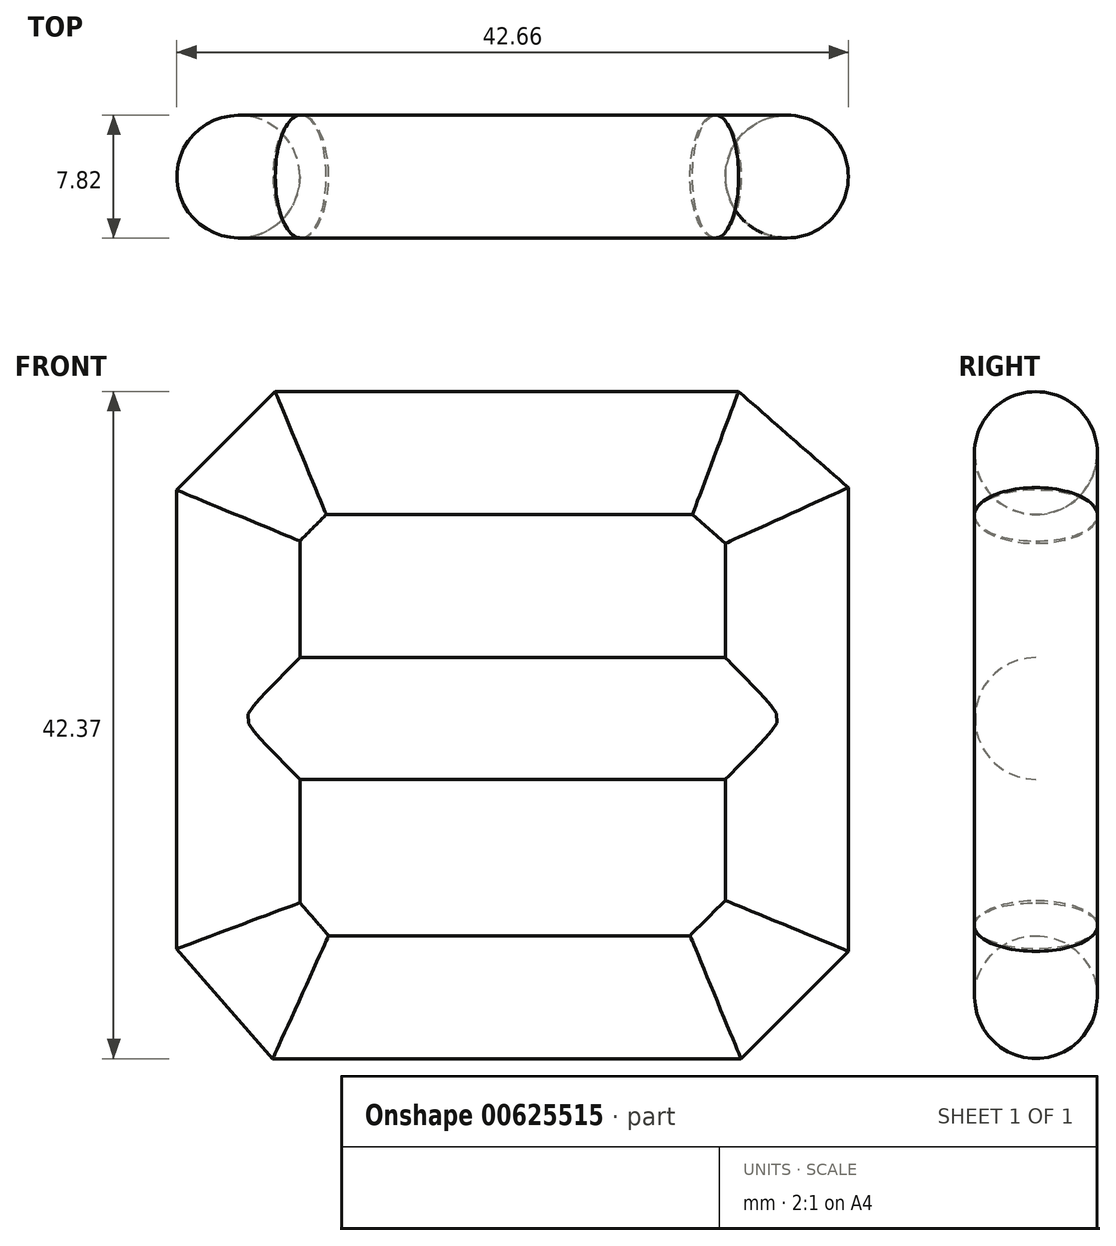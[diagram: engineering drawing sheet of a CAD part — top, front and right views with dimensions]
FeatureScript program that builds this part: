
annotation { "Feature Type Name" : "Feature", "Feature Type Description" : "" }
export const myFeature = defineFeature(function(context is Context, id is Id, definition is map)
    precondition{}
    {
        {
            var Q0;
            Q0=qCreatedBy(makeId("Top.planeOp"),FACE);
            var sketch = newSketch(context, id + "F0", { "sketchPlane" : qUnion([Q0])});
            skCircle(sketch, "E0", {"center": v(0, 0) * mm, "radius": 3.9 * mm});
            skSolve(sketch);
        }
        {
            var Q0;
            Q0=qCreatedBy(makeId("Front.planeOp"),FACE);
            var sketch = newSketch(context, id + "F1", { "sketchPlane" : qUnion([Q0])});
            skLineSegment(sketch, "E1", {"start": v(0, 0) * mm, "end": v(0, -13.17) * mm});
            skLineSegment(sketch, "E2", {"start": v(0, -13.17) * mm, "end": v(3.97, -17.7) * mm});
            skLineSegment(sketch, "E3", {"start": v(3.97, -17.7) * mm, "end": v(30.31, -17.7) * mm});
            skLineSegment(sketch, "E4", {"start": v(30.31, -17.7) * mm, "end": v(34.84, -13.17) * mm});
            skLineSegment(sketch, "E5", {"start": v(34.84, -13.17) * mm, "end": v(34.84, 0) * mm});
            skLineSegment(sketch, "E6", {"start": v(34.84, 0) * mm, "end": v(34.84, 12.89) * mm});
            skLineSegment(sketch, "E7", {"start": v(34.84, 12.89) * mm, "end": v(30.31, 16.85) * mm});
            skLineSegment(sketch, "E8", {"start": v(30.31, 16.85) * mm, "end": v(3.97, 16.85) * mm});
            skLineSegment(sketch, "E9", {"start": v(3.97, 16.85) * mm, "end": v(0, 12.89) * mm});
            skLineSegment(sketch, "E10", {"start": v(0, 12.89) * mm, "end": v(0, 0) * mm});
            skLineSegment(sketch, "E11", {"start": v(34.84, 0) * mm, "end": v(0, 0) * mm});
            skLineSegment(sketch, "E12", {"start": v(11.33, 16.85) * mm, "end": v(11.33, -17.7) * mm});
            skLineSegment(sketch, "E13", {"start": v(11.33, -17.7) * mm, "end": v(23.51, -17.7) * mm});
            skLineSegment(sketch, "E14", {"start": v(23.51, -17.7) * mm, "end": v(23.51, 16.85) * mm});
            skSolve(sketch);
        }
        {
            var Q0;
            Q0=makeQuery(id+"F0.imprint","IMPRINT",FACE,{"disambiguationData":[TD([[makeQuery(id+"F0.imprint","IMPRINT",EDGE,{"derivedFrom":sQuery(id+"F0.wireOp",EDGE,"E0")}),1.0]])]});
            var Q1;
            Q1=sQuery(id+"F1.wireOp",EDGE,"E10");
            var Q2;
            Q2=sQuery(id+"F1.wireOp",EDGE,"E9");
            var Q3;
            Q3=sQuery(id+"F1.wireOp",EDGE,"E8");
            var Q4;
            Q4=sQuery(id+"F1.wireOp",EDGE,"E7");
            var Q5;
            Q5=sQuery(id+"F1.wireOp",EDGE,"E6");
            var Q6;
            Q6=sQuery(id+"F1.wireOp",EDGE,"E5");
            var Q7;
            Q7=sQuery(id+"F1.wireOp",EDGE,"E4");
            var Q8;
            Q8=sQuery(id+"F1.wireOp",EDGE,"E3");
            var Q9;
            Q9=sQuery(id+"F1.wireOp",EDGE,"E2");
            var Q10;
            Q10=sQuery(id+"F1.wireOp",EDGE,"E1");
            sweep(context, id + "F2", {"profiles" : qUnion([Q0]), "path" : qUnion([Q1, Q2, Q3, Q4, Q5, Q6, Q7, Q8, Q9, Q10])});
        }
        {
            var Q0;
            Q0=qCreatedBy(makeId("Right.planeOp"),FACE);
            var sketch = newSketch(context, id + "F3", { "sketchPlane" : qUnion([Q0])});
            skCircle(sketch, "E15", {"center": v(0, 0) * mm, "radius": 3.87 * mm});
            skSolve(sketch);
        }
        {
            var Q0;
            Q0=qCreatedBy(makeId("Front.planeOp"),FACE);
            var sketch = newSketch(context, id + "F4", { "sketchPlane" : qUnion([Q0])});
            skLineSegment(sketch, "E16", {"start": v(0, 0) * mm, "end": v(35.13, 0) * mm});
            skSolve(sketch);
        }
        {
            var Q0;
            Q0 = qSketchRegion(id + "F3", true);
            var Q1;
            Q1=sQuery(id+"F4.wireOp",EDGE,"E16");
            sweep(context, id + "F5", {"operationType" : NewBodyOperationType.ADD, "profiles" : qUnion([Q0]), "path" : qUnion([Q1])});
        }
    });
